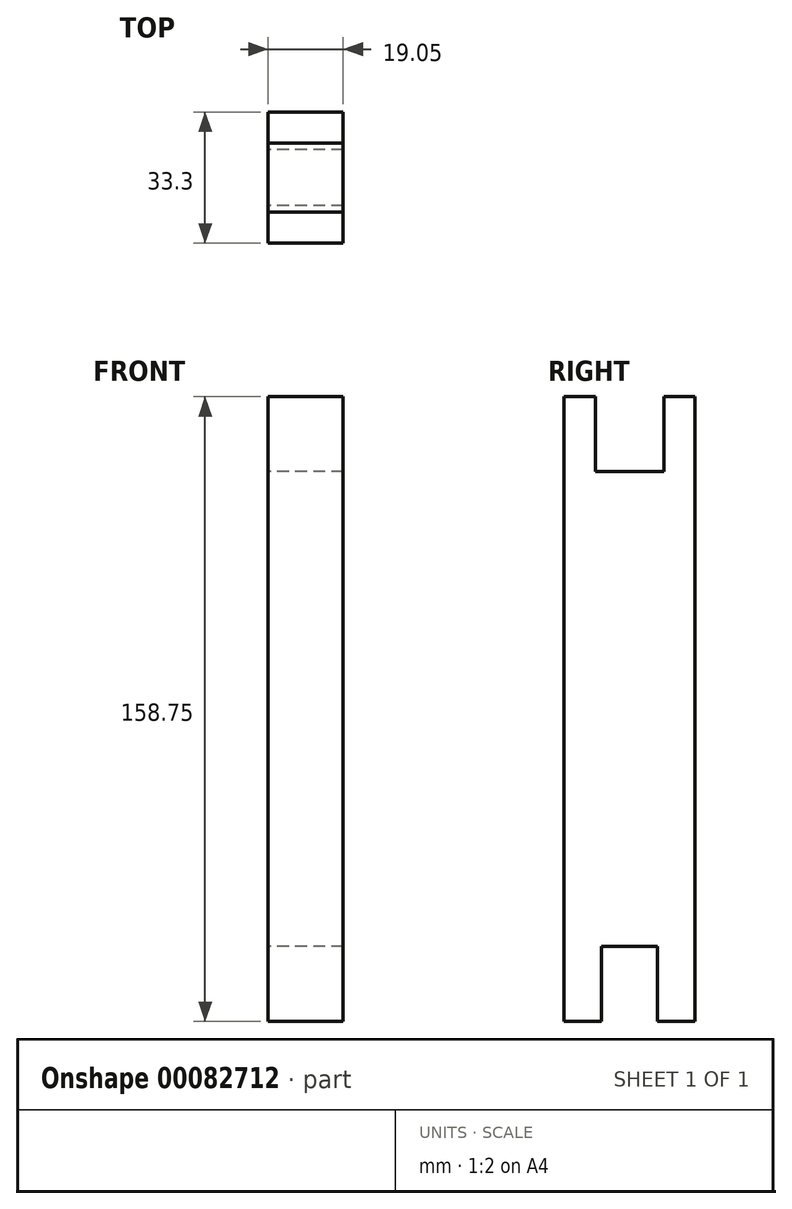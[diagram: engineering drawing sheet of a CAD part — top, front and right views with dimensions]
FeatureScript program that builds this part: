
annotation { "Feature Type Name" : "Feature", "Feature Type Description" : "" }
export const myFeature = defineFeature(function(context is Context, id is Id, definition is map)
    precondition{}
    {
        {
            var Q0;
            Q0=qCreatedBy(makeId("Right.planeOp"),FACE);
            var sketch = newSketch(context, id + "F0", { "sketchPlane" : qUnion([Q0])});
            skLineSegment(sketch, "E0", {"start": v(-50.77, 79.17) * mm, "end": v(-50.77, -79.58) * mm});
            skLineSegment(sketch, "E1", {"start": v(-50.77, 79.17) * mm, "end": v(-42.84, 79.17) * mm});
            skLineSegment(sketch, "E2", {"start": v(-42.84, 79.17) * mm, "end": v(-42.84, 60.12) * mm});
            skLineSegment(sketch, "E3", {"start": v(-42.84, 60.12) * mm, "end": v(-34.12, 60.12) * mm});
            skLineSegment(sketch, "E4", {"start": v(-50.77, -79.58) * mm, "end": v(-17.47, -79.58) * mm, "construction": true});
            skLineSegment(sketch, "E5", {"start": v(-50.77, -79.58) * mm, "end": v(-41.23, -79.58) * mm});
            skLineSegment(sketch, "E6", {"start": v(-41.23, -79.58) * mm, "end": v(-41.23, -60.53) * mm});
            skLineSegment(sketch, "E7", {"start": v(-41.23, -60.53) * mm, "end": v(-34.12, -60.53) * mm});
            skLineSegment(sketch, "E8.MirrorCS", {"start": v(-25.41, 60.12) * mm, "end": v(-34.12, 60.12) * mm});
            skLineSegment(sketch, "E9.MirrorCS", {"start": v(-25.41, 79.17) * mm, "end": v(-25.41, 60.12) * mm});
            skLineSegment(sketch, "E10.MirrorCS", {"start": v(-17.47, 79.17) * mm, "end": v(-25.41, 79.17) * mm});
            skLineSegment(sketch, "E11.MirrorCS", {"start": v(-17.47, 79.17) * mm, "end": v(-17.47, -79.58) * mm});
            skLineSegment(sketch, "E12.MirrorCS", {"start": v(-27.01, -60.53) * mm, "end": v(-34.12, -60.53) * mm});
            skLineSegment(sketch, "E13.MirrorCS", {"start": v(-27.01, -79.58) * mm, "end": v(-27.01, -60.53) * mm});
            skLineSegment(sketch, "E14.MirrorCS", {"start": v(-17.47, -79.58) * mm, "end": v(-27.01, -79.58) * mm});
            skSolve(sketch);
        }
        {
            var Q0;
            Q0=qSketchRegion(id+"F0",true);
            extrude(context, id + "F1", {"entities" : qUnion([Q0]), "depth" : 19.05 * mm});
        }
        {
            var Q0;
            Q0=qSketchRegion(id+"F0",true);
            extrude(context, id + "F2", {"entities" : qUnion([Q0]), "operationType" : NewBodyOperationType.ADD, "depth" : 9.52 * mm});
        }
    });
